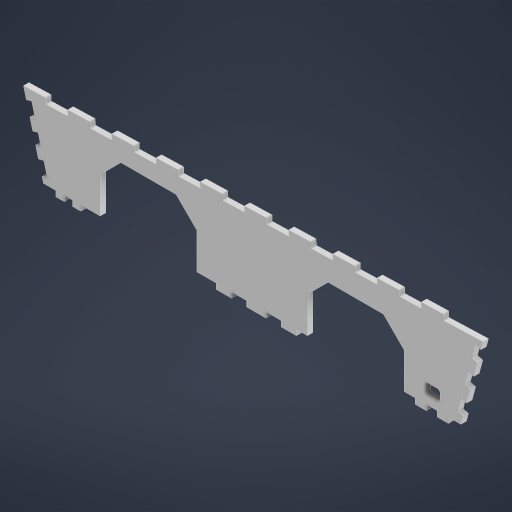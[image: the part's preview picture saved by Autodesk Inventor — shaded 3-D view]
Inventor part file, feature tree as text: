
AUTODESK INVENTOR PART (.ipt)
format: ipt  version: 2023.2 (Build 272271000, 271)  size: 417,792 bytes
history: native  units: mm
features: sketch x2
ambient origin geometry x8: Origin, YZ Plane, XZ Plane, XY Plane, X Axis, Y Axis, Z Axis, Center Point
bodies: Body1 (feature_tree)
feature tree (2):
  sketch  "Sketch1"  dims[d271=105.0deg]
  sketch  "Sketch2"  dims[d273=105.0deg d276=8.0mm d277=6.0mm d278=6.0mm d279=6.0mm d281=11.0mm d282=11.0mm d283=30.0mm d284=14.0mm d285=70.0mm d286=14.0mm d287=14.0mm d288=11.0mm d289=11.0mm d290=8.0mm d297=15.0mm d298=15.0mm d303=70.0mm d304=8.0mm d305=8.0mm d307=8.0mm d308=8.0mm d309=4.0mm d310=4.0mm d311=0.0mm d312=8.0mm d313=10.0mm d314=10.0mm d315=10.0mm d316=10.0mm d319=10.0mm d321=10.0mm d322=10.0mm d323=8.0mm d324=10.0mm d325=8.0mm d326=10.0mm d327=8.0mm d328=8.0mm d329=8.0mm d333=16.0mm d334=16.0mm d339=11.0mm d340=8.0mm d341=2.0mm d342=6.0mm d344=4.0mm d345=0.0mm d346=6.0mm d9=0.5mm d10=0.872665mm d11=0.5mm d12=0.872665mm d13=0.5mm d14=0.872665mm d27=0.5mm d28=0.872665mm d29=0.5mm d30=0.872665mm d88=0.5mm d89=0.872665mm d90=0.5mm d91=0.872665mm d116=0.5mm d117=0.872665mm d118=0.5mm d119=0.872665mm d154=0.5mm d155=0.872665mm d156=0.5mm d157=0.872665mm d181=0.5mm d182=0.872665mm d183=0.5mm d184=0.872665mm d221=0.5mm d222=0.872665mm d223=0.5mm d224=0.872665mm]
